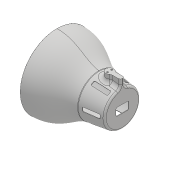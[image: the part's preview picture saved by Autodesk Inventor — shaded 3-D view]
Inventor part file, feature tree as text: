
AUTODESK INVENTOR PART (.ipt)
format: ipt  version: 2018 (Build 220112000, 112)  size: 544,256 bytes
history: native  units: mm
features: fillet x8, sketch x6, extrude x4, projected_geometry x2, revolve x1, shell x1, plane x1, hole x1, pattern_circular x1
ambient origin geometry x8: Origin, YZ Plane, XZ Plane, XY Plane, X Axis, Y Axis, Z Axis, Center Point
bodies: Solid1 (feature_tree)
feature tree (25):
  revolve  "Revolution1"  [1 undecoded]
  fillet  "Fillet1"  Radius=45.0mm
  shell  "Shell1"  Thickness=45.0mm
  fillet  "Fillet3"  Radius=10.0mm
  plane  "Work Plane1"
  extrude  "Extrusion1"  Depth=22.0mm
  hole  "Hole1"  [1 undecoded]
  extrude  "Extrusion3"  Depth=25.0mm
  fillet  "Fillet4"  Radius=1.0mm
  pattern_circular  "Circular Pattern1"  Count=5  [1 undecoded]
  extrude  "Extrusion4"  Depth=3.0mm
  fillet  "Fillet5"  Radius=10.0mm
  fillet  "Fillet6"  Radius=8.0mm
  fillet  "Fillet7"  Radius=30.0mm
  fillet  "Fillet8"  Radius=8.0mm
  extrude  "Extrusion5"  Depth=3.0mm
  fillet  "Fillet9"  [1 undecoded]
  sketch  "Sketch1"  dims[d0=125.0mm d1=40.0mm d2=45.0mm d3=45.0mm d4=10.0mm]
  sketch  "Sketch2"  dims[d5=70.0mm d6=22.0mm]
  sketch  "Sketch4"  dims[d7=70.0mm d8=90.0deg]
  projected_geometry  "Projected Loop2"
  sketch  "Sketch5"  dims[d9=17.104227mm d10=25.0mm d12=1.0mm]
  sketch  "Sketch6"  dims[d13=0.25mm d14=50.0mm]
  projected_geometry  "Projected Loop3"
  sketch  "Sketch8"  dims[d15=15.0mm d16=38.0mm d17=10.0mm d18=0.0mm d22=8.0mm d23=3.2mm d24=6.0mm d25=6.3mm d26=2.0mm d27=90.0deg d28=15.0mm d29=20.594885mm d30=30.0mm d31=8.0mm d32=40.0mm d33=0.0mm d34=0.0mm d35=2.0mm d36=60.0mm d37=360.0deg d39=20.0mm d40=10.0mm d41=0.0mm d42=8.0mm d43=8.0mm d44=3.0mm d45=3.5mm d55=15.0mm d56=25.0mm d57=10.0mm d58=0.0mm d59=3.0mm]
note: 4 required parameter values undecoded (feature->parameter linkage not recoverable at this tier; creation-order binding heuristic only, values carry confidence <= 0.55)